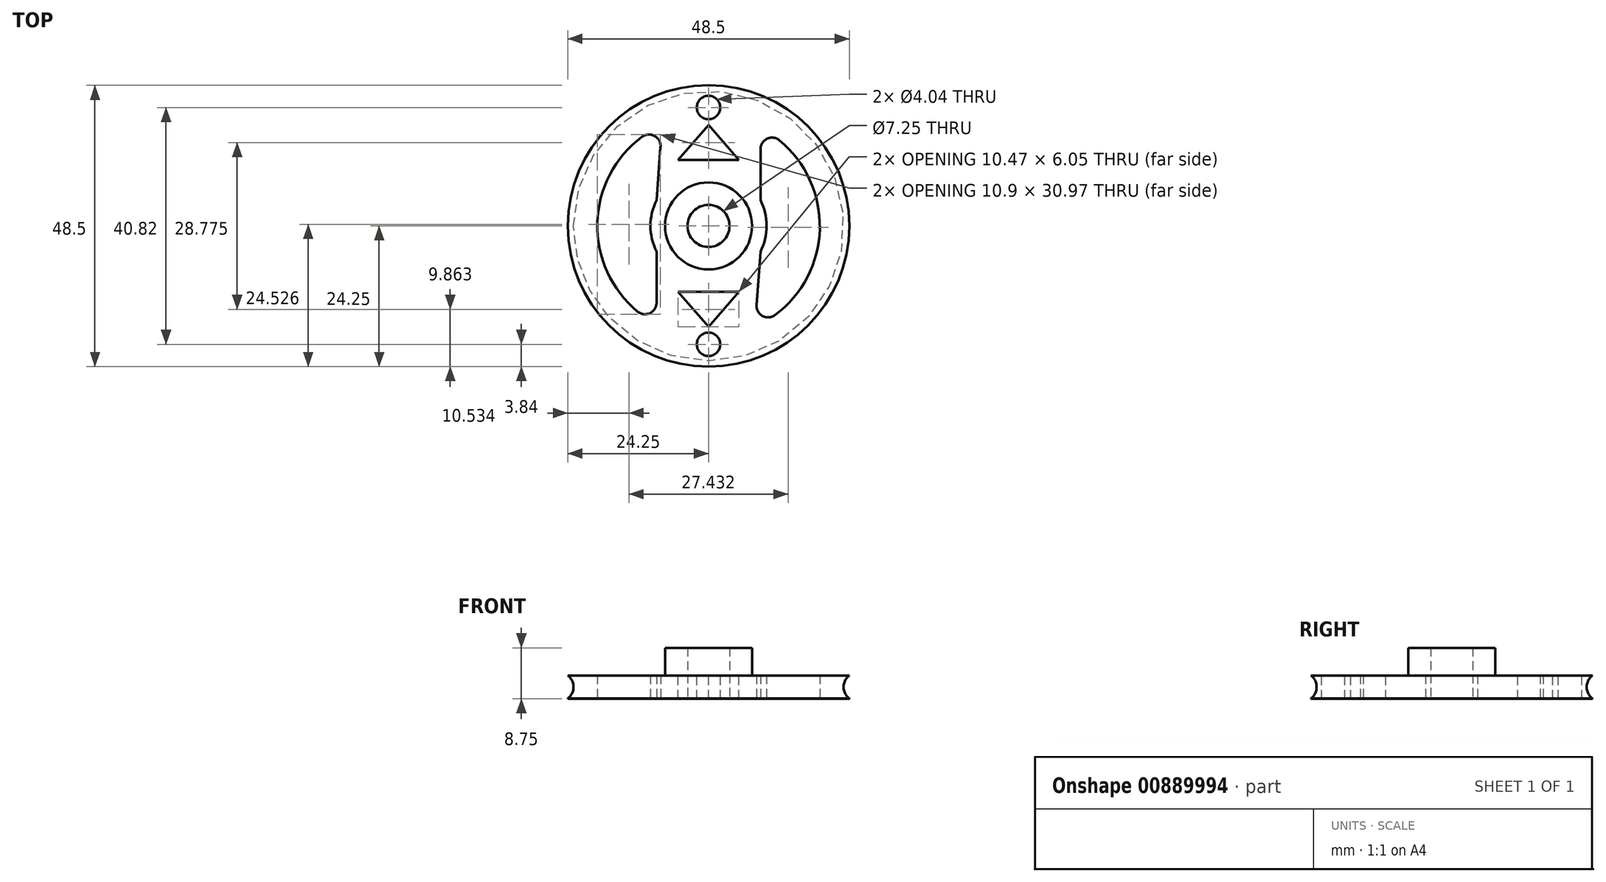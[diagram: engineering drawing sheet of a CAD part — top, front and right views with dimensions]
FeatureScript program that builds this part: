
annotation { "Feature Type Name" : "Feature", "Feature Type Description" : "" }
export const myFeature = defineFeature(function(context is Context, id is Id, definition is map)
    precondition{}
    {
        {
            var Q0;
            Q0=qCreatedBy(makeId("Top.planeOp"),FACE);
            var sketch = newSketch(context, id + "F0", { "sketchPlane" : qUnion([Q0])});
            skCircle(sketch, "E0", {"center": v(0, 0) * mm, "radius": 24.25 * mm});
            skCircle(sketch, "E1", {"center": v(0, 0) * mm, "radius": 3.63 * mm});
            skArc(sketch, "E2", {"start": v(-8.95, 4.46) * mm, "mid": v(-10, 0) * mm, "end": v(-8.95, -4.46) * mm});
            skArc(sketch, "E3.0", {"start": v(-11.46, 15.37) * mm, "mid": v(-19.16, 0.49) * mm, "end": v(-12.23, -14.77) * mm});
            skLineSegment(sketch, "E4.0", {"start": v(-8.27, 13.62) * mm, "end": v(-8.95, 4.46) * mm});
            skLineSegment(sketch, "E5.0", {"start": v(8.95, 13.23) * mm, "end": v(8.95, 4.46) * mm});
            skPoint(sketch, "E6.orphan", {"position": v(0, 22.46) * mm});
            skPoint(sketch, "E7.visualSharp", {"position": v(-7.98, 17.43) * mm});
            skArc(sketch, "E7.filletArc", {"start": v(-8.27, 13.62) * mm, "mid": v(-9.3, 15.52) * mm, "end": v(-11.46, 15.37) * mm});
            skPoint(sketch, "E8.visualSharp", {"position": v(8.95, 16.95) * mm});
            skArc(sketch, "E8.filletArc", {"start": v(12.23, 14.77) * mm, "mid": v(10.1, 15.04) * mm, "end": v(8.95, 13.23) * mm});
            skArc(sketch, "E9.1.0", {"start": v(-12.23, -14.77) * mm, "mid": v(-10.1, -15.04) * mm, "end": v(-8.95, -13.23) * mm});
            skArc(sketch, "E9.1.1", {"start": v(8.27, -13.62) * mm, "mid": v(9.3, -15.52) * mm, "end": v(11.46, -15.37) * mm});
            skLineSegment(sketch, "E9.1.2", {"start": v(8.27, -13.62) * mm, "end": v(8.95, -4.46) * mm});
            skLineSegment(sketch, "E9.1.3", {"start": v(-8.95, -13.23) * mm, "end": v(-8.95, -4.46) * mm});
            skArc(sketch, "E10.trimOffspring", {"start": v(11.46, -15.37) * mm, "mid": v(19.16, -0.49) * mm, "end": v(12.23, 14.77) * mm});
            skArc(sketch, "E11.trimOffspring", {"start": v(8.95, -4.46) * mm, "mid": v(10, 0) * mm, "end": v(8.95, 4.46) * mm});
            skSolve(sketch);
        }
        {
            var Q0;
            Q0=makeQuery(id+"F0.imprint","IMPRINT",FACE,{"disambiguationData":[TD([[makeQuery(id+"F0.imprint","IMPRINT",EDGE,{"derivedFrom":sQuery(id+"F0.wireOp",EDGE,"E0")}),1.0]])]});
            extrude(context, id + "F1", {"entities" : qUnion([Q0]), "depth" : 4 * mm, "offsetDistance" : 25.4 * mm});
        }
        {
            var Q0;
            Q0=makeQuery(id+"F1.opExtrude","CAP_FACE",FACE,{"disambiguationData":[OSD([sQuery(id+"F0.wireOp",EDGE,"E0"),sQuery(id+"F0.wireOp",EDGE,"E1"),sQuery(id+"F0.wireOp",EDGE,"E2"),sQuery(id+"F0.wireOp",EDGE,"E3.0"),sQuery(id+"F0.wireOp",EDGE,"E4.0"),sQuery(id+"F0.wireOp",EDGE,"E5.0"),sQuery(id+"F0.wireOp",EDGE,"E7.filletArc"),sQuery(id+"F0.wireOp",EDGE,"E8.filletArc"),sQuery(id+"F0.wireOp",EDGE,"E9.1.0"),sQuery(id+"F0.wireOp",EDGE,"E9.1.1"),sQuery(id+"F0.wireOp",EDGE,"E9.1.2"),sQuery(id+"F0.wireOp",EDGE,"E9.1.3"),sQuery(id+"F0.wireOp",EDGE,"E10.trimOffspring"),sQuery(id+"F0.wireOp",EDGE,"E11.trimOffspring")])],"isStart":false});
            var sketch = newSketch(context, id + "F2", { "sketchPlane" : qUnion([Q0])});
            skCircle(sketch, "E12", {"center": v(0, 0) * mm, "radius": 7.5 * mm});
            skSolve(sketch);
        }
        {
            var Q0;
            Q0=makeQuery(id+"F2.imprint","IMPRINT",FACE,{"disambiguationData":[TD([[makeQuery(id+"F2.imprint","IMPRINT",EDGE,{"derivedFrom":sQuery(id+"F2.wireOp",EDGE,"E12")}),1.0]])]});
            extrude(context, id + "F3", {"entities" : qUnion([Q0]), "operationType" : NewBodyOperationType.ADD, "depth" : 4.75 * mm, "offsetDistance" : 25.4 * mm});
        }
        {
            var Q0;
            Q0=makeQuery(id+"F1.opExtrude","CAP_FACE",FACE,{"disambiguationData":[OSD([sQuery(id+"F0.wireOp",EDGE,"E0"),sQuery(id+"F0.wireOp",EDGE,"E1"),sQuery(id+"F0.wireOp",EDGE,"E2"),sQuery(id+"F0.wireOp",EDGE,"E3.0"),sQuery(id+"F0.wireOp",EDGE,"E4.0"),sQuery(id+"F0.wireOp",EDGE,"E5.0"),sQuery(id+"F0.wireOp",EDGE,"E7.filletArc"),sQuery(id+"F0.wireOp",EDGE,"E8.filletArc"),sQuery(id+"F0.wireOp",EDGE,"E9.1.0"),sQuery(id+"F0.wireOp",EDGE,"E9.1.1"),sQuery(id+"F0.wireOp",EDGE,"E9.1.2"),sQuery(id+"F0.wireOp",EDGE,"E9.1.3"),sQuery(id+"F0.wireOp",EDGE,"E10.trimOffspring"),sQuery(id+"F0.wireOp",EDGE,"E11.trimOffspring")])],"isStart":false});
            var sketch = newSketch(context, id + "F4", { "sketchPlane" : qUnion([Q0])});
            skLineSegment(sketch, "E13", {"start": v(0, 11.36) * mm, "end": v(-5.23, 11.36) * mm});
            skLineSegment(sketch, "E14", {"start": v(-5.23, 11.36) * mm, "end": v(0, 17.41) * mm});
            skLineSegment(sketch, "E15", {"start": v(0, 17.41) * mm, "end": v(0, 11.36) * mm});
            skLineSegment(sketch, "E16.MirrorCS", {"start": v(0, 11.36) * mm, "end": v(5.23, 11.36) * mm});
            skLineSegment(sketch, "E17.MirrorCS", {"start": v(5.23, 11.36) * mm, "end": v(0, 17.41) * mm});
            skLineSegment(sketch, "E18.1.0", {"start": v(-5.23, -11.36) * mm, "end": v(0, -17.41) * mm});
            skLineSegment(sketch, "E18.1.1", {"start": v(5.23, -11.36) * mm, "end": v(0, -17.41) * mm});
            skLineSegment(sketch, "E18.1.2", {"start": v(0, -11.36) * mm, "end": v(-5.23, -11.36) * mm});
            skLineSegment(sketch, "E18.1.3", {"start": v(0, -11.36) * mm, "end": v(5.23, -11.36) * mm});
            skPoint(sketch, "E18.center", {"position": v(0, 0) * mm});
            skCircle(sketch, "E19", {"center": v(0, 20.41) * mm, "radius": 2.02 * mm});
            skCircle(sketch, "E20.1.0", {"center": v(0, -20.41) * mm, "radius": 2.02 * mm});
            skSolve(sketch);
        }
        {
            var Q0;
            Q0=qSketchRegion(id+"F4",true);
            extrude(context, id + "F5", {"entities" : qUnion([Q0]), "operationType" : NewBodyOperationType.REMOVE, "endBound" : BoundingType.THROUGH_ALL, "oppositeDirection" : true, "depth" : 25.4 * mm, "offsetDistance" : 25.4 * mm});
        }
        {
            var Q0;
            Q0=qCreatedBy(makeId("Front.planeOp"),FACE);
            var sketch = newSketch(context, id + "F6", { "sketchPlane" : qUnion([Q0])});
            skCircle(sketch, "E21", {"center": v(-25.77, 2.01) * mm, "radius": 2.5 * mm});
            skLineSegment(sketch, "E22", {"start": v(0, 14.96) * mm, "end": v(0, -0.92) * mm, "construction": true});
            skSolve(sketch);
        }
        {
            var Q0;
            Q0=qSketchRegion(id+"F6",true);
            var Q1;
            Q1=sQuery(id+"F6.wireOp",EDGE,"E22");
            revolve(context, id + "F7", {"operationType" : NewBodyOperationType.REMOVE, "surfaceOperationType" : NewSurfaceOperationType.NEW, "entities" : qUnion([Q0]), "axis" : qUnion([Q1]), "revolveType" : RevolveType.FULL, "oppositeDirection" : true});
        }
    });
